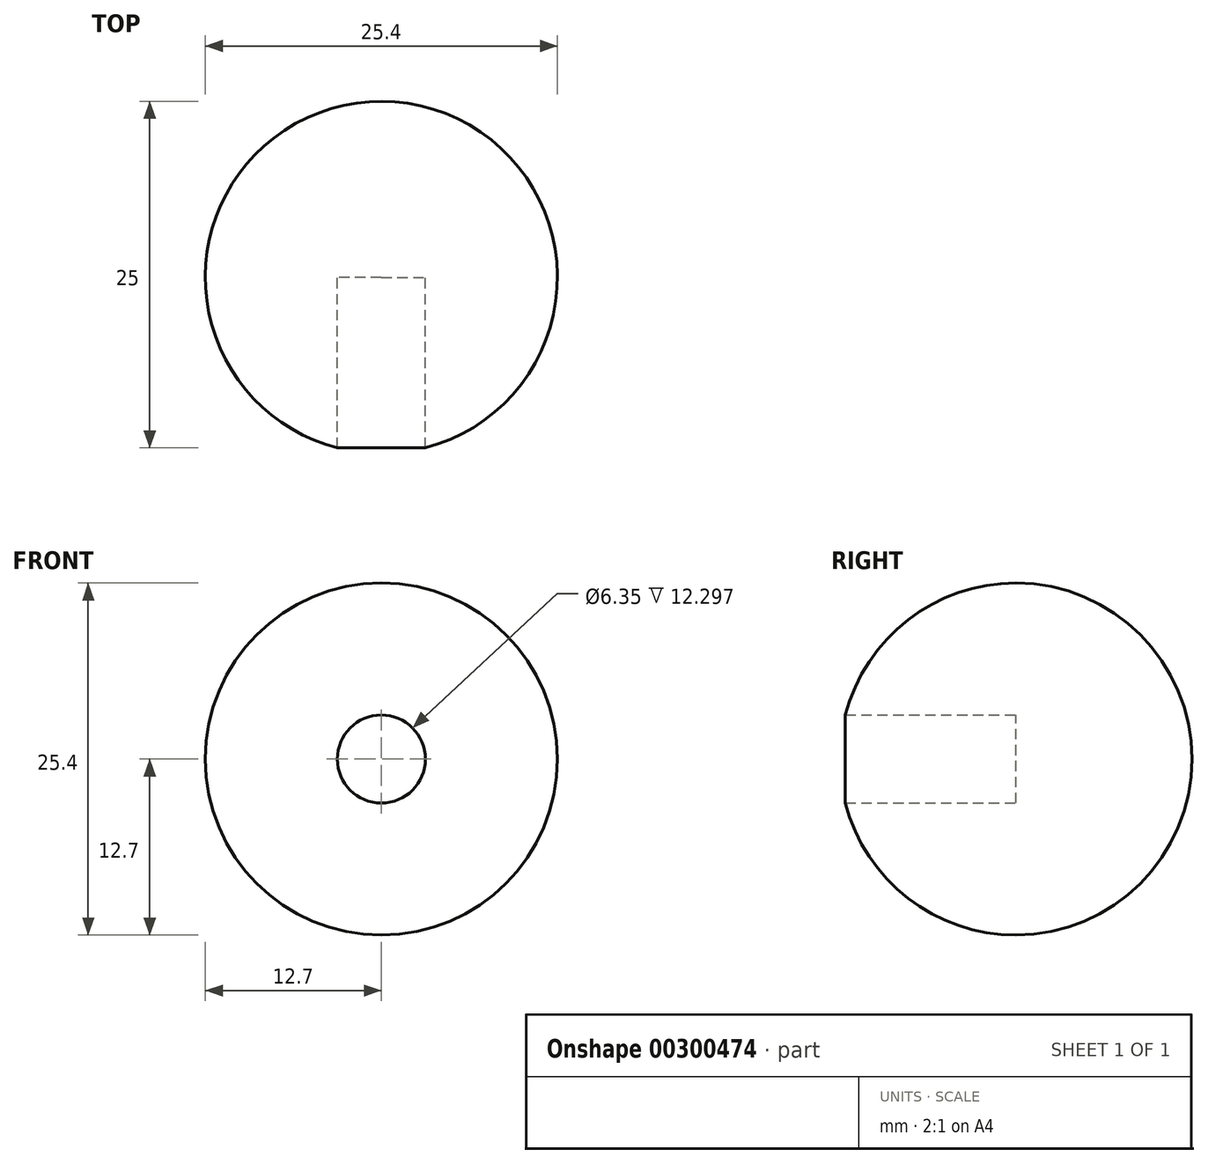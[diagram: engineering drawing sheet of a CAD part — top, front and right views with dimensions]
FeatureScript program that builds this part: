
annotation { "Feature Type Name" : "Feature", "Feature Type Description" : "" }
export const myFeature = defineFeature(function(context is Context, id is Id, definition is map)
    precondition{}
    {
        {
            var Q0;
            Q0=qCreatedBy(makeId("Front.planeOp"),FACE);
            var sketch = newSketch(context, id + "F0", { "sketchPlane" : qUnion([Q0])});
            skArc(sketch, "E0", {"start": v(0, 12.7) * mm, "mid": v(-12.7, 0) * mm, "end": v(0, -12.7) * mm});
            skLineSegment(sketch, "E1", {"start": v(0, 12.7) * mm, "end": v(0, -12.7) * mm});
            skSolve(sketch);
        }
        {
            var Q0;
            Q0=qCreatedBy(makeId("Top.planeOp"),FACE);
            var sketch = newSketch(context, id + "F1", { "sketchPlane" : qUnion([Q0])});
            skCircle(sketch, "E2", {"center": v(0, 0) * mm, "radius": 12.7 * mm});
            skSolve(sketch);
        }
        {
            var Q0;
            Q0=makeQuery(id+"F0.imprint","IMPRINT",FACE,{"disambiguationData":[TD([[makeQuery(id+"F0.imprint","IMPRINT",EDGE,{"derivedFrom":sQuery(id+"F0.wireOp",EDGE,"E0")}),1.0]])]});
            var Q1;
            Q1=sQuery(id+"F1.wireOp",EDGE,"E2");
            revolve(context, id + "F2", {"entities" : qUnion([Q0]), "axis" : qUnion([Q1]), "revolveType" : RevolveType.FULL});
        }
        {
            var Q0;
            Q0=qCreatedBy(makeId("Front.planeOp"),FACE);
            cPlane(context, id + "F3", {"entities" : qUnion([Q0]), "cplaneType" : CPlaneType.OFFSET, "offset" : 6.35 * mm, "width" : 152.4 * mm, "height" : 152.4 * mm});
        }
        {
            var Q0;
            Q0=qCreatedBy(makeId("Front.planeOp"),FACE);
            var sketch = newSketch(context, id + "F4", { "sketchPlane" : qUnion([Q0])});
            skCircle(sketch, "E3", {"center": v(0, 0) * mm, "radius": 3.18 * mm});
            skSolve(sketch);
        }
        {
            var Q0;
            Q0 = qSketchRegion(id + "F4", true);
            extrude(context, id + "F5", {"entities" : qUnion([Q0]), "operationType" : NewBodyOperationType.REMOVE, "depth" : 52.83 * mm});
        }
    });
